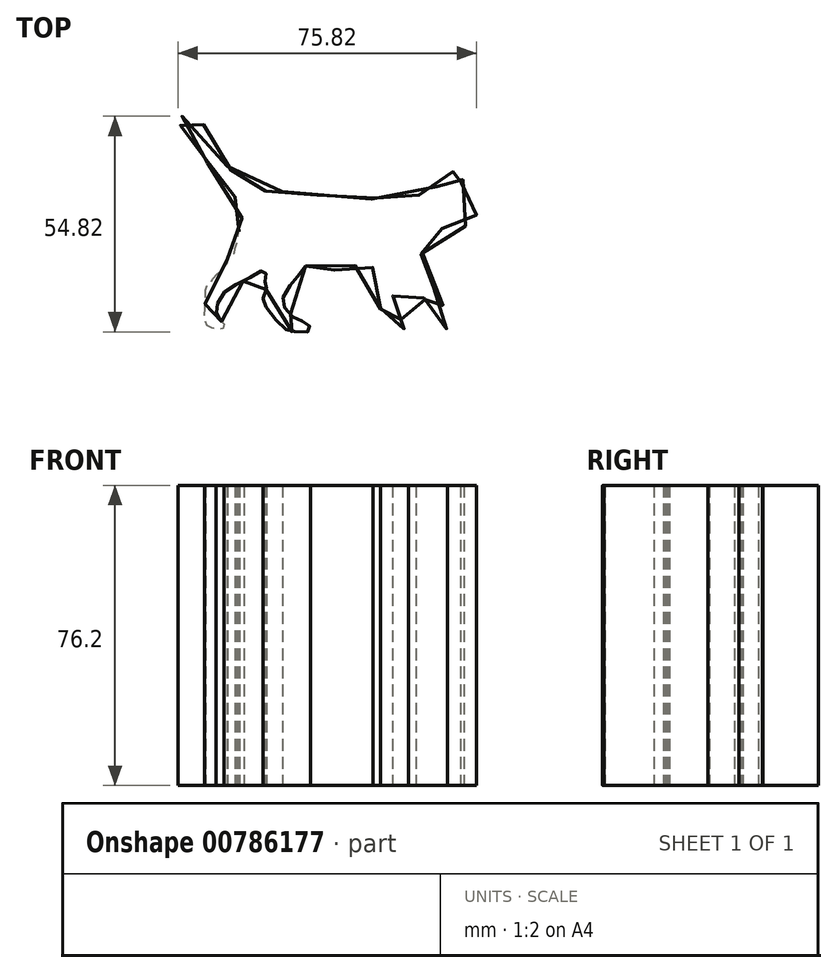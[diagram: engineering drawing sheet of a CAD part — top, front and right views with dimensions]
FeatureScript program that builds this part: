
annotation { "Feature Type Name" : "Feature", "Feature Type Description" : "" }
export const myFeature = defineFeature(function(context is Context, id is Id, definition is map)
    precondition{}
    {
        {
            var Q0;
            Q0=qCreatedBy(makeId("Top.planeOp"),FACE);
            var sketch = newSketch(context, id + "F0", { "sketchPlane" : qUnion([Q0])});
            skFitSpline(sketch, "E0", {"points": [v(-43.68, 17.03) * mm, v(-44.75, 15.58) * mm, v(-46.31, 13.8) * mm, v(-46.94, 13.14) * mm, v(-48.54, 10.46) * mm, v(-49.32, 9.06) * mm, v(-49.5, 8.31) * mm, v(-49.35, 7.02) * mm, v(-47.83, 5.12) * mm, v(-46.76, 3.97) * mm, v(-45.83, 3.2) * mm, v(-44.72, 3.05) * mm, v(-43.57, 2.53) * mm, v(-42.82, 2) * mm, v(-42.5, 1.38) * mm, v(-42.42, 0.67) * mm, v(-42.97, 0.34) * mm, v(-44.9, 0.3) * mm, v(-46.87, 0.34) * mm, v(-47.68, 0.41) * mm, v(-48.5, 0.86) * mm, v(-49.65, 1.75) * mm, v(-51.76, 3.97) * mm, v(-53.7, 6.6) * mm, v(-54.3, 7.61) * mm, v(-54.5, 8.2) * mm, v(-54.22, 9.58) * mm, v(-53.73, 10.84) * mm, v(-53.6, 11.94) * mm, v(-53.75, 12.43) * mm, v(-53.98, 12.94) * mm, v(-53.82, 13.34) * mm, v(-53.63, 13.69) * mm, v(-53.68, 14.58) * mm, v(-53.73, 16.17) * mm, v(-54.05, 16.3) * mm, v(-55.52, 15.35) * mm, v(-57.14, 14.4) * mm, v(-59.75, 13.14) * mm, v(-62.13, 11.93) * mm, v(-63.98, 10.7) * mm, v(-65.49, 8.84) * mm, v(-66.12, 7.29) * mm, v(-66.28, 6.84) * mm, v(-66.35, 5.32) * mm, v(-66.12, 4.71) * mm, v(-65.7, 3.83) * mm, v(-64.94, 2.86) * mm, v(-64.48, 2.35) * mm, v(-64.4, 1.39) * mm, v(-65.17, 0.98) * mm, v(-66.4, 1) * mm, v(-67.64, 1.3) * mm, v(-68.61, 1.92) * mm, v(-69, 2.89) * mm, v(-69.3, 3.55) * mm, v(-69.28, 5.14) * mm, v(-69.17, 7.67) * mm, v(-69.03, 10.92) * mm, v(-68.97, 11.64) * mm, v(-68.3, 12.36) * mm, v(-67.72, 12.78) * mm, v(-67.58, 13.4) * mm, v(-66.7, 14.34) * mm, v(-64.72, 16.42) * mm, v(-63.58, 17.7) * mm, v(-63.55, 18.78) * mm, v(-62.2, 20) * mm, v(-61.55, 20.76) * mm, v(-61.6, 21.65) * mm, v(-61.27, 21.98) * mm, v(-61.36, 22.59) * mm, v(-60.86, 23.48) * mm, v(-60.92, 24.67) * mm, v(-60.42, 25.48) * mm, v(-60.83, 26.13) * mm, v(-60.17, 28.63) * mm, v(-59.61, 29.81) * mm, v(-59.43, 30.87) * mm, v(-59.36, 32.18) * mm, v(-61.64, 34.66) * mm, v(-64.12, 36.94) * mm, v(-66.16, 39.45) * mm, v(-67.9, 42.2) * mm, v(-69.42, 44.68) * mm, v(-70.01, 46.27) * mm, v(-70.98, 48.29) * mm, v(-71.8, 49.78) * mm, v(-73.82, 51.7) * mm, v(-75.7, 52.96) * mm, v(-76.05, 54.32) * mm, v(-75.42, 54.98) * mm, v(-73.4, 55.05) * mm, v(-71.64, 54.77) * mm, v(-69.94, 53.5) * mm, v(-69.07, 51.9) * mm, v(-67.5, 48.63) * mm, v(-65.35, 44.77) * mm, v(-63.1, 41.89) * mm, v(-61.23, 39.89) * mm, v(-58.81, 37.68) * mm, v(-57.22, 36.74) * mm, v(-55.25, 36.18) * mm, v(-53.92, 36.06) * mm, v(-52.72, 35.8) * mm, v(-49.86, 35.91) * mm, v(-46.74, 35.91) * mm, v(-41.5, 35.12) * mm, v(-37.47, 34.62) * mm, v(-31.12, 33.8) * mm, v(-27.53, 33.98) * mm, v(-24.24, 34.69) * mm, v(-22.53, 35.22) * mm, v(-20.53, 35.4) * mm, v(-17.37, 35.04) * mm, v(-15.37, 34.98) * mm, v(-12.4, 35.73) * mm, v(-10.1, 37.35) * mm, v(-9.06, 37.82) * mm, v(-7.62, 39.26) * mm, v(-6.31, 40.96) * mm, v(-5.87, 41.1) * mm, v(-5.56, 40.76) * mm, v(-5.42, 39.93) * mm, v(-5, 40.01) * mm, v(-4.23, 40.7) * mm, v(-3.76, 40.9) * mm, v(-3.53, 40.51) * mm, v(-3.62, 39.2) * mm, v(-4.28, 37.2) * mm, v(-3.42, 36.32) * mm, v(-1.98, 34.79) * mm, v(-1.64, 33.57) * mm, v(-0.5, 31.62) * mm, v(-0.3, 29.73) * mm, v(-1.03, 28.06) * mm, v(-2.95, 27.15) * mm, v(-4.95, 27.37) * mm, v(-7.34, 27.34) * mm, v(-9.31, 26.42) * mm, v(-9.92, 26.26) * mm, v(-10.83, 25.38) * mm, v(-11.65, 23.61) * mm, v(-12.94, 22.11) * mm, v(-13.56, 20.73) * mm, v(-14.48, 19.82) * mm, v(-14.6, 19.05) * mm, v(-15.5, 17.67) * mm, v(-15.21, 16.25) * mm, v(-13.27, 13.82) * mm, v(-11.22, 11.7) * mm, v(-10.62, 10.74) * mm, v(-8.96, 7.33) * mm, v(-8.08, 5.27) * mm, v(-7.56, 2.33) * mm, v(-8.15, 0.75) * mm, v(-9.28, 0.86) * mm, v(-10.26, 1.94) * mm, v(-10.85, 2.64) * mm, v(-12.32, 6.39) * mm, v(-14.14, 9.4) * mm, v(-18.27, 11.74) * mm, v(-20.76, 13.32) * mm, v(-21.07, 12.9) * mm, v(-21.35, 10.9) * mm, v(-21.39, 5.8) * mm, v(-19.53, 3.45) * mm, v(-18.13, 2.68) * mm, v(-17.5, 1.84) * mm, v(-17.75, 1.35) * mm, v(-19.32, 0.96) * mm, v(-21.39, 1.1) * mm, v(-22.79, 1.77) * mm, v(-23.49, 3.17) * mm, v(-23.66, 4.5) * mm, v(-24.58, 6.1) * mm, v(-24.58, 8.24) * mm, v(-24.93, 10.17) * mm, v(-25.45, 12.27) * mm, v(-26.57, 15.84) * mm, v(-26.6, 16.54) * mm, v(-27.13, 17.2) * mm, v(-29.13, 17.28) * mm, v(-31.2, 17.1) * mm, v(-33.19, 17.24) * mm, v(-35.81, 16.37) * mm, v(-36.93, 15.8) * mm, v(-37.63, 16.5) * mm, v(-38.44, 16.33) * mm, v(-39.67, 16.47) * mm, v(-41.17, 16.54) * mm, v(-41.73, 16.9) * mm, v(-43.68, 17.03) * mm]});
            skSolve(sketch);
        }
        {
            var Q0;
            Q0 = qSketchRegion(id + "F0", true);
            extrude(context, id + "F1", {"entities" : qUnion([Q0]), "depth" : 76.2 * mm, "offsetDistance" : 25.4 * mm});
        }
    });
